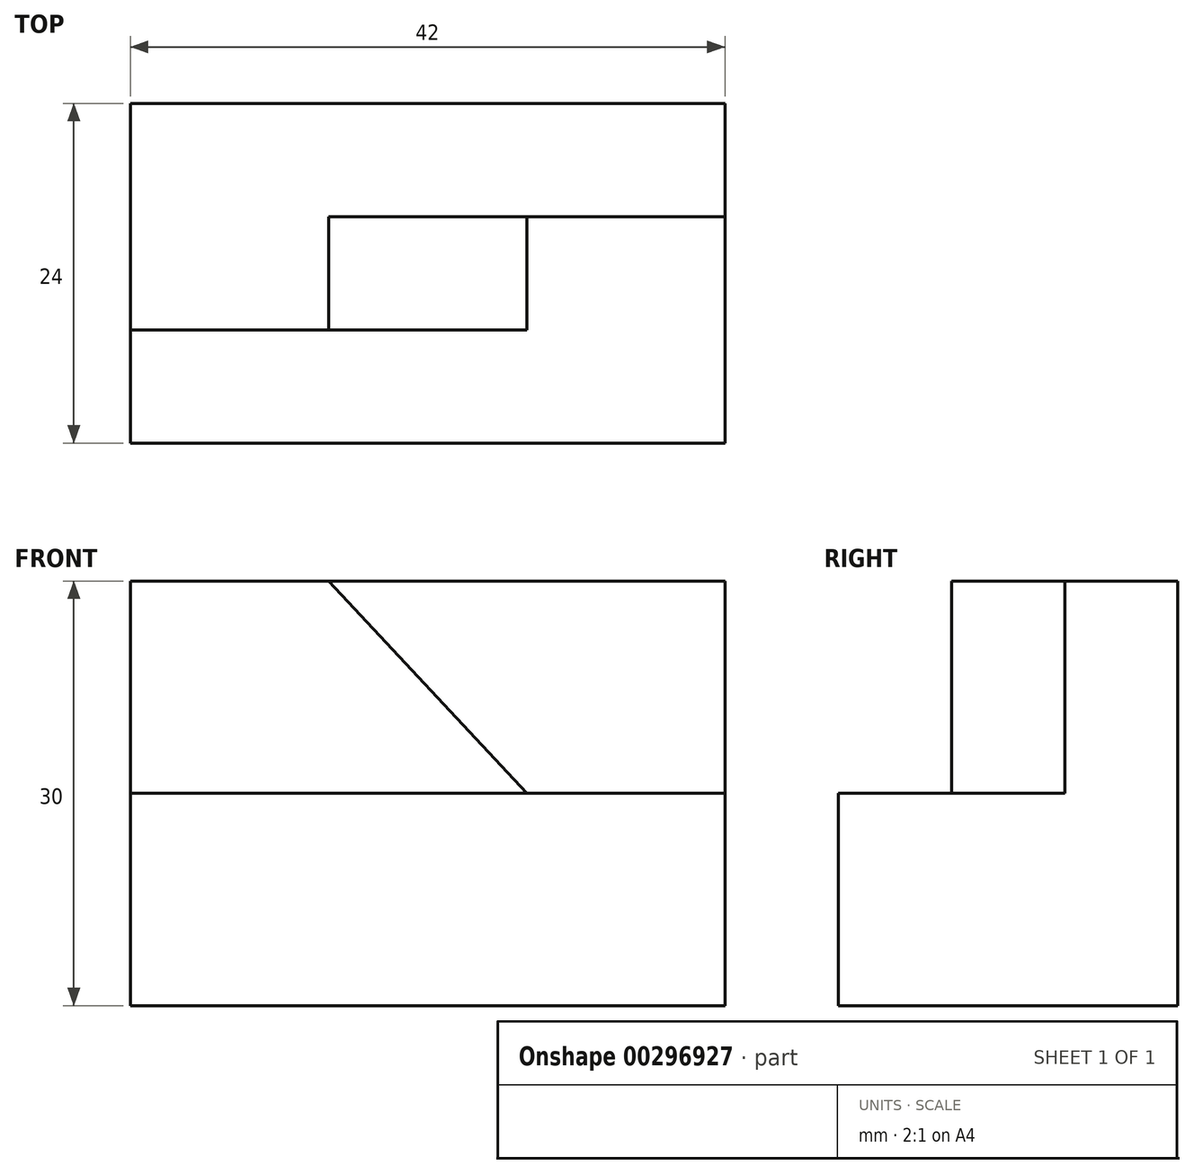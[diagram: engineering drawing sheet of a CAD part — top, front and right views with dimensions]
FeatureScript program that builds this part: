
annotation { "Feature Type Name" : "Feature", "Feature Type Description" : "" }
export const myFeature = defineFeature(function(context is Context, id is Id, definition is map)
    precondition{}
    {
        {
            var Q0;
            Q0=qCreatedBy(makeId("Front.planeOp"),FACE);
            var sketch = newSketch(context, id + "F0", { "sketchPlane" : qUnion([Q0])});
            skLineSegment(sketch, "E0.bottom", {"start": v(0, 0) * mm, "end": v(42, 0) * mm});
            skLineSegment(sketch, "E0.top", {"start": v(0, 30) * mm, "end": v(42, 30) * mm});
            skLineSegment(sketch, "E0.left", {"start": v(0, 0) * mm, "end": v(0, 30) * mm});
            skLineSegment(sketch, "E0.right", {"start": v(42, 0) * mm, "end": v(42, 30) * mm});
            skLineSegment(sketch, "E1", {"start": v(0, 15) * mm, "end": v(42, 15) * mm});
            skLineSegment(sketch, "E2", {"start": v(14, 30) * mm, "end": v(28, 15) * mm});
            skSolve(sketch);
        }
        {
            var Q0;
            Q0 = qSketchRegion(id + "F0", true);
            extrude(context, id + "F1", {"entities" : qUnion([Q0]), "oppositeDirection" : true, "depth" : 24 * mm});
        }
        {
            var Q0;
            {var subQ3=sQuery(id+"F0.wireOp",EDGE,"E2");Q0=makeQuery(id+"F0.imprint","IMPRINT",FACE,{"disambiguationData":[TD([[makeQuery(id+"F0.imprint","IMPRINT",EDGE,{"derivedFrom":subQ3}),-1.0]])]});}
            var Q1;
            {var subQ3=sQuery(id+"F0.wireOp",EDGE,"E2");Q1=makeQuery(id+"F0.imprint","IMPRINT",FACE,{"disambiguationData":[TD([[makeQuery(id+"F0.imprint","IMPRINT",EDGE,{"derivedFrom":subQ3}),1.0]])]});}
            extrude(context, id + "F2", {"entities" : qUnion([Q0, Q1]), "operationType" : NewBodyOperationType.REMOVE, "oppositeDirection" : true, "depth" : 8 * mm});
        }
        {
            var Q0;
            {var subQ3=sQuery(id+"F0.wireOp",EDGE,"E2");Q0=makeQuery(id+"F0.imprint","IMPRINT",FACE,{"disambiguationData":[TD([[makeQuery(id+"F0.imprint","IMPRINT",EDGE,{"derivedFrom":subQ3}),1.0]])]});}
            extrude(context, id + "F3", {"entities" : qUnion([Q0]), "operationType" : NewBodyOperationType.REMOVE, "oppositeDirection" : true, "depth" : 16 * mm});
        }
    });
